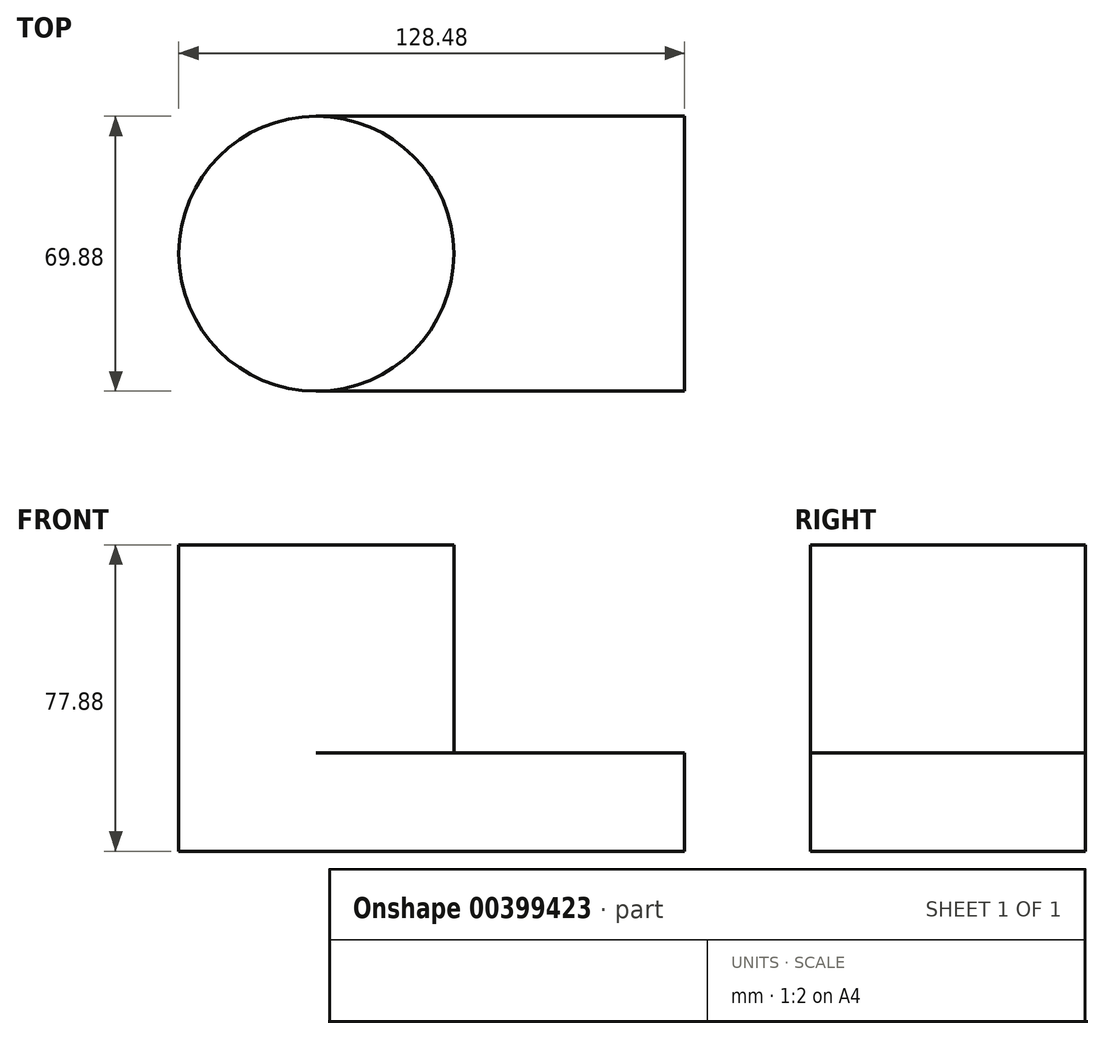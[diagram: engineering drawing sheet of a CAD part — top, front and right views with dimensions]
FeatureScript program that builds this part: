
annotation { "Feature Type Name" : "Feature", "Feature Type Description" : "" }
export const myFeature = defineFeature(function(context is Context, id is Id, definition is map)
    precondition{}
    {
        {
            var Q0;
            Q0=qCreatedBy(makeId("Top.planeOp"),FACE);
            var sketch = newSketch(context, id + "F0", { "sketchPlane" : qUnion([Q0])});
            skLineSegment(sketch, "E0.bottom", {"start": v(96.19, 34.94) * mm, "end": v(46.22, 34.94) * mm});
            skLineSegment(sketch, "E0.top", {"start": v(96.19, -34.94) * mm, "end": v(46.22, -34.94) * mm});
            skLineSegment(sketch, "E0.left", {"start": v(96.19, 34.94) * mm, "end": v(96.19, -34.94) * mm});
            skLineSegment(sketch, "E0.right", {"start": v(46.22, 34.94) * mm, "end": v(46.22, -34.94) * mm});
            skPoint(sketch, "E0.middle", {"position": v(71.2, 0) * mm});
            skCircle(sketch, "E1", {"center": v(46.22, 0) * mm, "radius": 34.94 * mm});
            skSolve(sketch);
        }
        {
            var Q0;
            {var subQ0=sQuery(id+"F0.wireOp",EDGE,"E0.bottom");Q0=makeQuery(id+"F0.imprint","IMPRINT",FACE,{"disambiguationData":[TD([[makeQuery(id+"F0.imprint","IMPRINT",EDGE,{"derivedFrom":subQ0}),1.0]])]});}
            var Q1;
            {var subQ0=sQuery(id+"F0.wireOp",EDGE,"E0.right");Q1=makeQuery(id+"F0.imprint","IMPRINT",FACE,{"disambiguationData":[TD([[makeQuery(id+"F0.imprint","IMPRINT",EDGE,{"derivedFrom":subQ0}),-1.0]])]});}
            var Q2;
            {var subQ0=sQuery(id+"F0.wireOp",EDGE,"E0.right");Q2=makeQuery(id+"F0.imprint","IMPRINT",FACE,{"disambiguationData":[TD([[makeQuery(id+"F0.imprint","IMPRINT",EDGE,{"derivedFrom":subQ0}),1.0]])]});}
            extrude(context, id + "F1", {"entities" : qUnion([Q0, Q1, Q2]), "depth" : 25 * mm});
        }
        {
            var Q0;
            {var subQ0=sQuery(id+"F0.wireOp",EDGE,"E0.right");Q0=makeQuery(id+"F0.imprint","IMPRINT",FACE,{"disambiguationData":[TD([[makeQuery(id+"F0.imprint","IMPRINT",EDGE,{"derivedFrom":subQ0}),1.0]])]});}
            var Q1;
            {var subQ0=sQuery(id+"F0.wireOp",EDGE,"E0.right");Q1=makeQuery(id+"F0.imprint","IMPRINT",FACE,{"disambiguationData":[TD([[makeQuery(id+"F0.imprint","IMPRINT",EDGE,{"derivedFrom":subQ0}),-1.0]])]});}
            var Q2;
            Q2=sQuery(id+"F0.wireOp",EDGE,"E1");
            extrude(context, id + "F2", {"entities" : qUnion([Q0, Q1]), "operationType" : NewBodyOperationType.ADD, "surfaceEntities" : qUnion([Q2]), "depth" : 77.88 * mm});
        }
        {
            var Q0;
            Q0=makeQuery(id+"F1.opExtrude","SWEPT_FACE",FACE,{"disambiguationData":[OSD([sQuery(id+"F0.wireOp",EDGE,"E0.left")])]});
            extrude(context, id + "F3", {"entities" : qUnion([Q0]), "operationType" : NewBodyOperationType.ADD, "depth" : 43.57 * mm});
        }
    });
